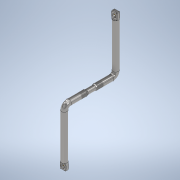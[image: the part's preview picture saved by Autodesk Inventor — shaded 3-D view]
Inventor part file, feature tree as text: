
AUTODESK INVENTOR PART (.ipt)
format: ipt  version: 2021 (Build 250183000, 183)  size: 1,568,768 bytes
history: native  units: mm
features: sketch x14, other x5, plane x4, fillet x3, thread x2, sweep x2, loft x2, hole x2, revolve x1
ambient origin geometry x8: Origin, YZ Plane, XZ Plane, XY Plane, X Axis, Y Axis, Z Axis, Center Point
bodies: Body1 (feature_tree)
feature tree (35):
  other  "Sólido1"
  revolve  "Revolución1"  [1 undecoded]
  thread  "Rosca1"  [1 undecoded]
  thread  "Rosca2"  [1 undecoded]
  sketch  "Boceto2"  dims[d9=25.0mm d10=0.0mm d14=2100.0mm]
  sketch  "Boceto4"  dims[d24=190.678642mm d25=190.678642mm]
  other  "Punto de trabajo1"
  sketch  "Boceto5"  dims[d32=20.0mm d33=15.0mm d34=230.0mm]
  sweep  "Barrido1"
  sketch  "Boceto8"  dims[d39=0.0mm d40=0.0mm d42=40.0mm]
  sweep  "Barrido2"
  plane  "Plano de trabajo2"
  sketch  "Boceto10"  dims[d43=20.0mm d45=27.0mm d46=14.0mm]
  plane  "Plano de trabajo3"
  loft  "Solevación3"
  fillet  "Empalme1"  Radius=230.0mm
  other  "Punto de trabajo2"
  hole  "Agujero1"  [1 undecoded]
  fillet  "Empalme2"  Radius=15.0mm
  plane  "Plano de trabajo5"
  loft  "Solevación4"
  other  "Punto de trabajo3"
  hole  "Agujero2"  [1 undecoded]
  fillet  "Empalme3"  Radius=14.0mm
  sketch  "Boceto1"  dims[d4=90.0deg d5=24.0mm d6=20.0mm d7=25.0mm d8=0.0mm]
  other  "Imagen1"
  sketch  "Boceto6"  dims[d35=0.0mm d36=0.0mm d37=230.0mm d38=15.0mm]
  sketch  "Boceto11"  dims[d47=15.0mm]
  sketch  "Boceto12"  dims[d59=14.0mm]
  sketch  "Boceto13"  dims[d67=14.0mm]
  plane  "Plano de trabajo4"
  sketch  "Boceto14"  dims[d68=0.0mm d69=90.0deg]
  sketch  "Boceto15"  dims[d70=0.0mm d71=90.0deg]
  sketch  "Boceto16"  dims[d72=0.0mm d73=90.0deg]
  sketch  "Boceto17"  dims[d74=2.0mm d75=16.0mm d76=32.0mm d77=4.0mm d78=2.0mm d79=90.0deg d80=8.0mm d81=20.594885mm d82=2.0mm d83=15.0mm d84=27.0mm d85=14.0mm d86=14.0mm d87=14.0mm d88=0.0mm d89=90.0deg d90=0.0mm d91=90.0deg d92=0.0mm d93=90.0deg d94=16.0mm d95=32.0mm d96=27.25mm d97=9.25mm d98=90.0deg d99=8.0mm d100=20.594885mm d101=2.0mm]
note: 5 required parameter values undecoded (feature->parameter linkage not recoverable at this tier; creation-order binding heuristic only, values carry confidence <= 0.55)